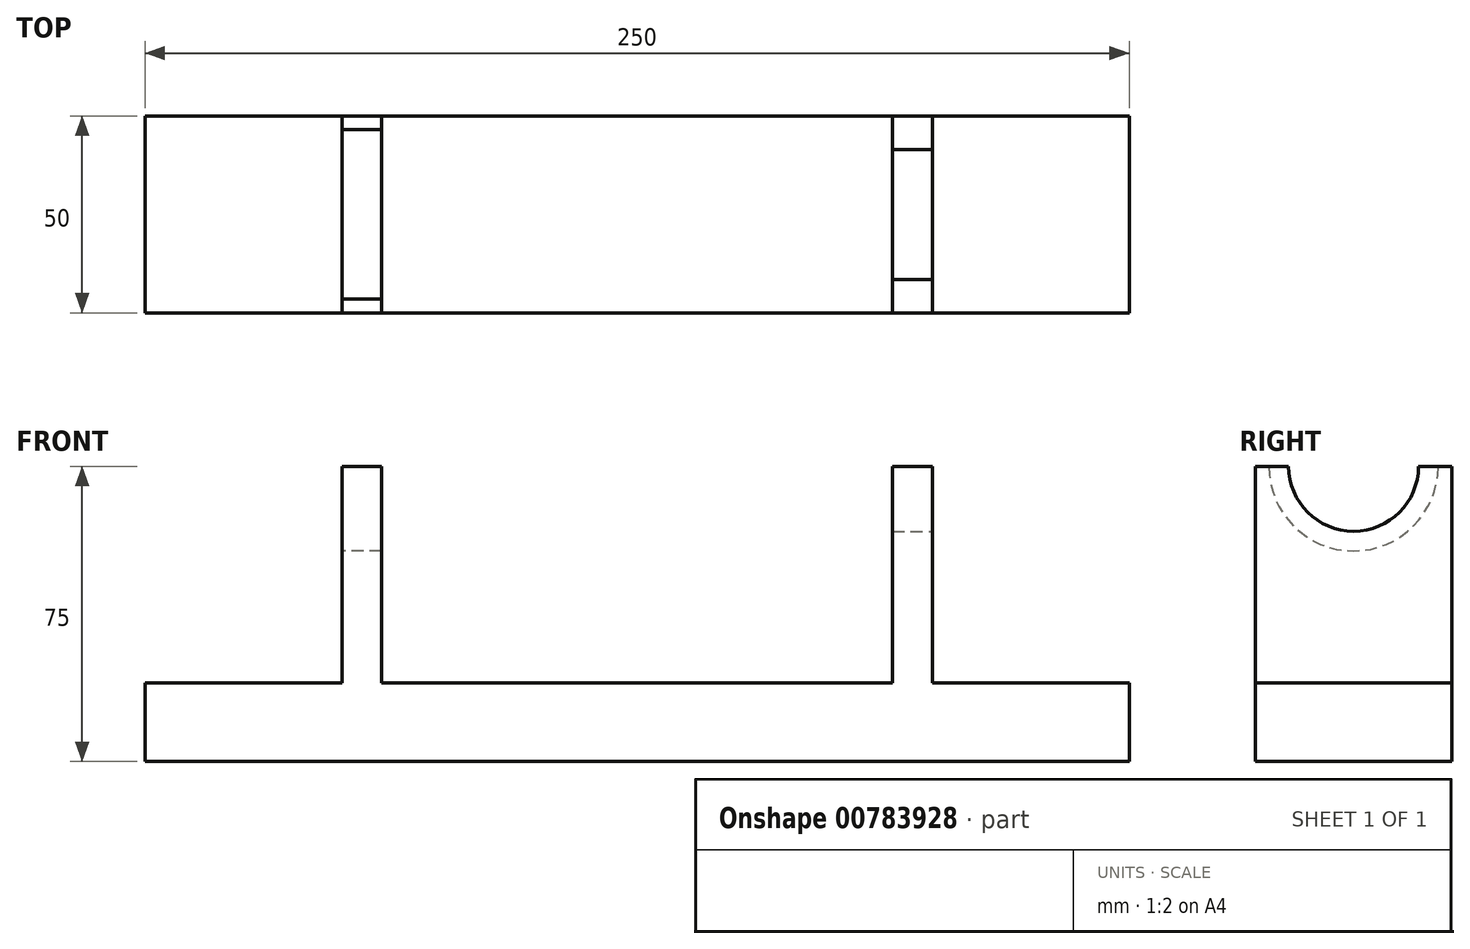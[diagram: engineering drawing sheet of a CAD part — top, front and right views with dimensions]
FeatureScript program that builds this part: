
annotation { "Feature Type Name" : "Feature", "Feature Type Description" : "" }
export const myFeature = defineFeature(function(context is Context, id is Id, definition is map)
    precondition{}
    {
        {
            var Q0;
            Q0=qCreatedBy(makeId("Top.planeOp"),FACE);
            var sketch = newSketch(context, id + "F0", { "sketchPlane" : qUnion([Q0])});
            skLineSegment(sketch, "E0.bottom", {"start": v(-122.7, -22.15) * mm, "end": v(127.3, -22.15) * mm});
            skLineSegment(sketch, "E0.top", {"start": v(-122.7, -72.15) * mm, "end": v(127.3, -72.15) * mm});
            skLineSegment(sketch, "E0.left", {"start": v(-122.7, -22.15) * mm, "end": v(-122.7, -72.15) * mm});
            skLineSegment(sketch, "E0.right", {"start": v(127.3, -22.15) * mm, "end": v(127.3, -72.15) * mm});
            skSolve(sketch);
        }
        {
            var Q0;
            Q0=makeQuery(id+"F0.imprint","IMPRINT",FACE,{"disambiguationData":[TD([[makeQuery(id+"F0.imprint","IMPRINT",EDGE,{"derivedFrom":sQuery(id+"F0.wireOp",EDGE,"E0.bottom")}),-1.0]])]});
            extrude(context, id + "F1", {"entities" : qUnion([Q0]), "depth" : 20 * mm, "offsetDistance" : 25 * mm});
        }
        {
            var Q0;
            Q0=makeQuery(id+"F1.opExtrude","CAP_FACE",FACE,{"disambiguationData":[OSD([sQuery(id+"F0.wireOp",EDGE,"E0.bottom"),sQuery(id+"F0.wireOp",EDGE,"E0.top"),sQuery(id+"F0.wireOp",EDGE,"E0.left"),sQuery(id+"F0.wireOp",EDGE,"E0.right")])],"isStart":false});
            var sketch = newSketch(context, id + "F2", { "sketchPlane" : qUnion([Q0])});
            skLineSegment(sketch, "E1", {"start": v(127.3, -22.15) * mm, "end": v(77.3, -22.15) * mm});
            skLineSegment(sketch, "E2.bottom", {"start": v(77.3, -22.15) * mm, "end": v(67.15, -22.15) * mm});
            skLineSegment(sketch, "E2.top", {"start": v(77.3, -72.15) * mm, "end": v(67.15, -72.15) * mm});
            skLineSegment(sketch, "E2.left", {"start": v(77.3, -22.15) * mm, "end": v(77.3, -72.15) * mm});
            skLineSegment(sketch, "E2.right", {"start": v(67.15, -22.15) * mm, "end": v(67.15, -72.15) * mm});
            skSolve(sketch);
        }
        {
            var Q0;
            Q0=makeQuery(id+"F2.imprint","IMPRINT",FACE,{"disambiguationData":[TD([[makeQuery(id+"F2.imprint","IMPRINT",EDGE,{"derivedFrom":sQuery(id+"F2.wireOp",EDGE,"E2.bottom")}),-1.0]])]});
            extrude(context, id + "F3", {"entities" : qUnion([Q0]), "operationType" : NewBodyOperationType.ADD, "depth" : 55 * mm, "offsetDistance" : 25 * mm});
        }
        {
            var Q0;
            Q0=makeQuery(id+"F3.opExtrude","SWEPT_FACE",FACE,{"disambiguationData":[OSD([sQuery(id+"F2.wireOp",EDGE,"E2.left")])]});
            var sketch = newSketch(context, id + "F4", { "sketchPlane" : qUnion([Q0])});
            skCircle(sketch, "E3", {"center": v(-47.15, 75) * mm, "radius": 16.5 * mm});
            skSolve(sketch);
        }
        {
            var Q0;
            {var subQ0=sQuery(id+"F4.wireOp",EDGE,"E3");var subQ1=makeQuery(id+"F3.opExtrude","CAP_EDGE",EDGE,{"disambiguationData":[OSD([sQuery(id+"F2.wireOp",EDGE,"E2.left")])],"isStart":false});var subQ2=makeQuery(id+"F4.imprint","INTERSECT",VERTEX,{"disambiguationData":[OD(0.0)],"derivedFrom":[subQ1,subQ0]});Q0=makeQuery(id+"F4.imprint","IMPRINT",FACE,{"disambiguationData":[TD([[makeQuery(id+"F4.imprint","IMPRINT",EDGE,{"disambiguationData":[TD([[subQ2,1.0]])],"derivedFrom":subQ0}),1.0]])]});}
            extrude(context, id + "F5", {"entities" : qUnion([Q0]), "operationType" : NewBodyOperationType.REMOVE, "endBound" : BoundingType.THROUGH_ALL, "oppositeDirection" : true, "depth" : 25 * mm, "offsetDistance" : 25 * mm});
        }
        {
            var Q0;
            {var subQ0=sQuery(id+"F0.wireOp",EDGE,"E0.left");var subQ1=sQuery(id+"F0.wireOp",EDGE,"E0.top");var subQ2=sQuery(id+"F0.wireOp",EDGE,"E0.bottom");Q0=makeQuery(id+"F3.boolean.opBoolean","SPLIT",FACE,{"disambiguationData":[TD([makeQuery(id+"F1.opExtrude","SWEPT_FACE",FACE,{"disambiguationData":[OSD([subQ0])]})])],"derivedFrom":makeQuery(id+"F1.opExtrude","CAP_FACE",FACE,{"disambiguationData":[OSD([subQ2,subQ1,subQ0,sQuery(id+"F0.wireOp",EDGE,"E0.right")])],"isStart":false})});}
            var sketch = newSketch(context, id + "F6", { "sketchPlane" : qUnion([Q0])});
            skLineSegment(sketch, "E4", {"start": v(-122.7, -72.15) * mm, "end": v(-72.7, -72.15) * mm});
            skLineSegment(sketch, "E5.bottom", {"start": v(-72.7, -72.15) * mm, "end": v(-60.65, -72.15) * mm});
            skLineSegment(sketch, "E5.top", {"start": v(-72.7, -22.15) * mm, "end": v(-60.65, -22.15) * mm});
            skLineSegment(sketch, "E5.left", {"start": v(-72.7, -72.15) * mm, "end": v(-72.7, -22.15) * mm});
            skLineSegment(sketch, "E5.right", {"start": v(-60.65, -72.15) * mm, "end": v(-60.65, -22.15) * mm});
            skSolve(sketch);
        }
        {
            var Q0;
            Q0=makeQuery(id+"F6.imprint","IMPRINT",FACE,{"disambiguationData":[TD([[makeQuery(id+"F6.imprint","IMPRINT",EDGE,{"derivedFrom":sQuery(id+"F6.wireOp",EDGE,"E5.bottom")}),1.0]])]});
            var Q1;
            {var subQ0=sQuery(id+"F2.wireOp",EDGE,"E2.left");var subQ1=sQuery(id+"F2.wireOp",EDGE,"E2.top");var subQ2=sQuery(id+"F2.wireOp",EDGE,"E2.right");Q1=makeQuery(id+"F5.boolean.opBoolean","SPLIT",FACE,{"disambiguationData":[TD([makeQuery(id+"F1.opExtrude","SWEPT_FACE",FACE,{"disambiguationData":[OSD([sQuery(id+"F0.wireOp",EDGE,"E0.top")])]})])],"derivedFrom":makeQuery(id+"F3.opExtrude","CAP_FACE",FACE,{"disambiguationData":[OSD([sQuery(id+"F2.wireOp",EDGE,"E2.bottom"),subQ1,subQ0,subQ2])],"isStart":false})});}
            extrude(context, id + "F7", {"entities" : qUnion([Q0]), "operationType" : NewBodyOperationType.ADD, "endBound" : BoundingType.UP_TO_SURFACE, "depth" : 25 * mm, "endBoundEntityFace" : qUnion([Q1]), "offsetDistance" : 25 * mm});
        }
        {
            var Q0;
            Q0=makeQuery(id+"F7.opExtrude","SWEPT_FACE",FACE,{"disambiguationData":[OSD([sQuery(id+"F6.wireOp",EDGE,"E5.left")])]});
            var sketch = newSketch(context, id + "F8", { "sketchPlane" : qUnion([Q0])});
            skCircle(sketch, "E6", {"center": v(47.15, 75) * mm, "radius": 21.5 * mm});
            skSolve(sketch);
        }
        {
            var Q0;
            {var subQ0=sQuery(id+"F8.wireOp",EDGE,"E6");var subQ1=makeQuery(id+"F7.opExtrude","CAP_EDGE",EDGE,{"disambiguationData":[OSD([sQuery(id+"F6.wireOp",EDGE,"E5.left")])],"isStart":false});var subQ2=makeQuery(id+"F8.imprint","INTERSECT",VERTEX,{"disambiguationData":[OD(0.0)],"derivedFrom":[subQ1,subQ0]});Q0=makeQuery(id+"F8.imprint","IMPRINT",FACE,{"disambiguationData":[TD([[makeQuery(id+"F8.imprint","IMPRINT",EDGE,{"disambiguationData":[TD([[subQ2,1.0]])],"derivedFrom":subQ0}),1.0]])]});}
            extrude(context, id + "F9", {"entities" : qUnion([Q0]), "operationType" : NewBodyOperationType.REMOVE, "endBound" : BoundingType.UP_TO_NEXT, "oppositeDirection" : true, "depth" : 25 * mm, "offsetDistance" : 25 * mm});
        }
        {
            var Q0;
            Q0=makeQuery(id+"F7.opExtrude","SWEPT_FACE",FACE,{"disambiguationData":[OSD([sQuery(id+"F6.wireOp",EDGE,"E5.right")])]});
            extrude(context, id + "F10", {"entities" : qUnion([Q0]), "operationType" : NewBodyOperationType.REMOVE, "oppositeDirection" : true, "depth" : 2 * mm, "offsetDistance" : 25 * mm});
        }
    });
